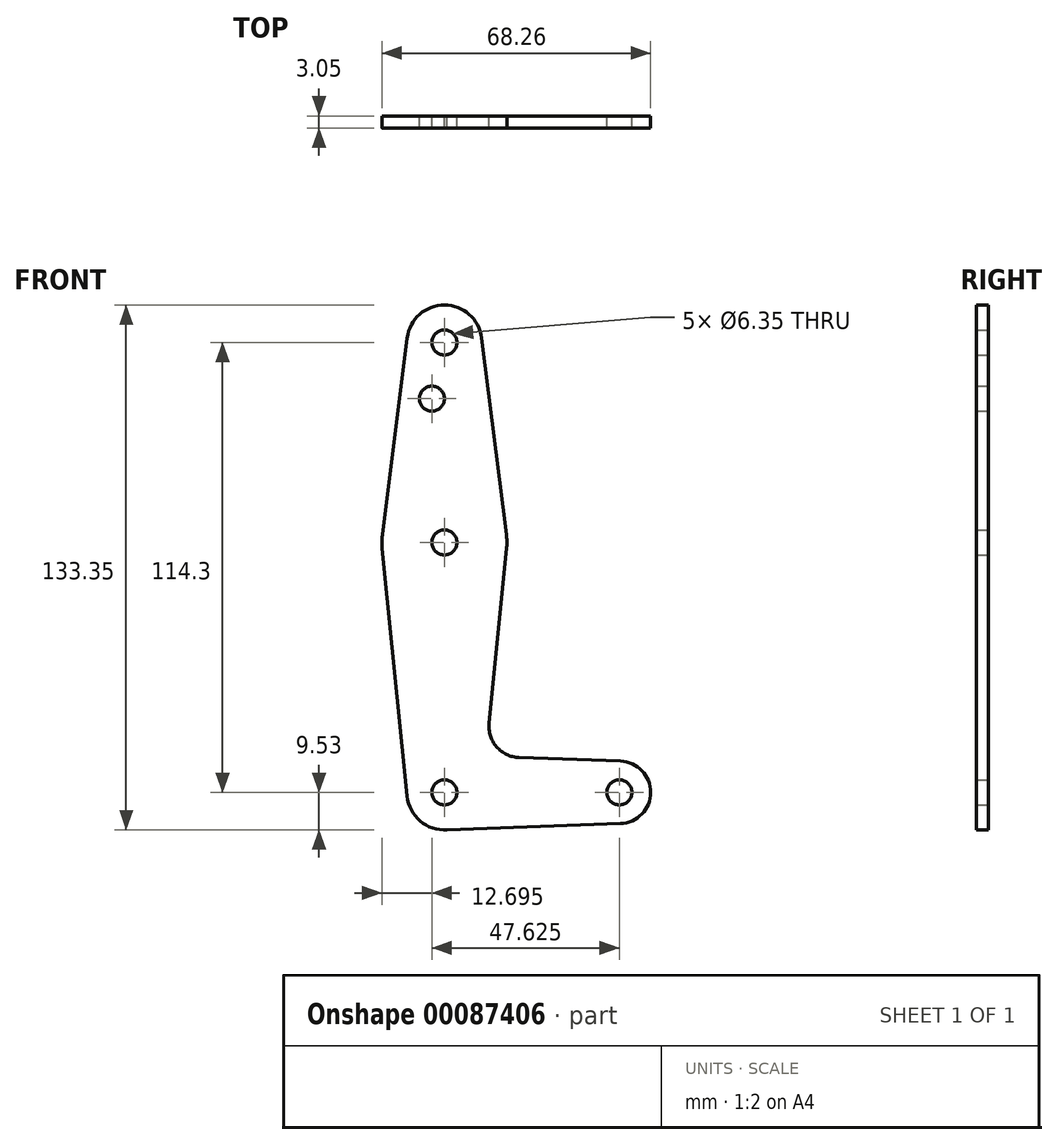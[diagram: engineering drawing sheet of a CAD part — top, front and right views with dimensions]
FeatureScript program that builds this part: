
annotation { "Feature Type Name" : "Feature", "Feature Type Description" : "" }
export const myFeature = defineFeature(function(context is Context, id is Id, definition is map)
    precondition{}
    {
        {
            var Q0;
            Q0=qCreatedBy(makeId("Front.planeOp"),FACE);
            var sketch = newSketch(context, id + "F0", { "sketchPlane" : qUnion([Q0])});
            skLineSegment(sketch, "E0", {"start": v(0, 50.8) * mm, "end": v(0, -63.5) * mm, "construction": true});
            skLineSegment(sketch, "E1", {"start": v(0, -63.5) * mm, "end": v(44.45, -63.5) * mm, "construction": true});
            skCircle(sketch, "E2", {"center": v(0, -63.5) * mm, "radius": 9.53 * mm});
            skCircle(sketch, "E3", {"center": v(44.45, -63.5) * mm, "radius": 7.94 * mm});
            skCircle(sketch, "E4", {"center": v(0, 0) * mm, "radius": 15.88 * mm});
            skCircle(sketch, "E5", {"center": v(0, 50.8) * mm, "radius": 9.53 * mm});
            skLineSegment(sketch, "E6", {"start": v(9.45, 52) * mm, "end": v(15.75, 1.98) * mm});
            skLineSegment(sketch, "E7", {"start": v(-9.45, 52) * mm, "end": v(-15.75, 1.98) * mm});
            skLineSegment(sketch, "E8", {"start": v(15.8, -1.59) * mm, "end": v(11.34, -45.9) * mm});
            skLineSegment(sketch, "E9", {"start": v(-15.8, -1.59) * mm, "end": v(-9.48, -64.45) * mm});
            skLineSegment(sketch, "E10", {"start": v(18.97, -54.65) * mm, "end": v(44.73, -55.57) * mm});
            skLineSegment(sketch, "E11", {"start": v(0, -73.03) * mm, "end": v(44.73, -71.43) * mm});
            skCircle(sketch, "E12", {"center": v(0, 50.8) * mm, "radius": 3.18 * mm});
            skCircle(sketch, "E13", {"center": v(0, 0) * mm, "radius": 3.18 * mm});
            skCircle(sketch, "E14", {"center": v(0, -63.5) * mm, "radius": 3.18 * mm});
            skCircle(sketch, "E15", {"center": v(44.45, -63.5) * mm, "radius": 3.18 * mm});
            skCircle(sketch, "E16", {"center": v(-3.18, 36.53) * mm, "radius": 3.18 * mm});
            skArc(sketch, "E17.filletArc", {"start": v(11.34, -45.9) * mm, "mid": v(13.26, -51.93) * mm, "end": v(18.97, -54.65) * mm});
            skSolve(sketch);
        }
        {
            var Q0;
            Q0 = qSketchRegion(id + "F0", true);
            extrude(context, id + "F1", {"entities" : qUnion([Q0]), "depth" : 3.05 * mm});
        }
    });
